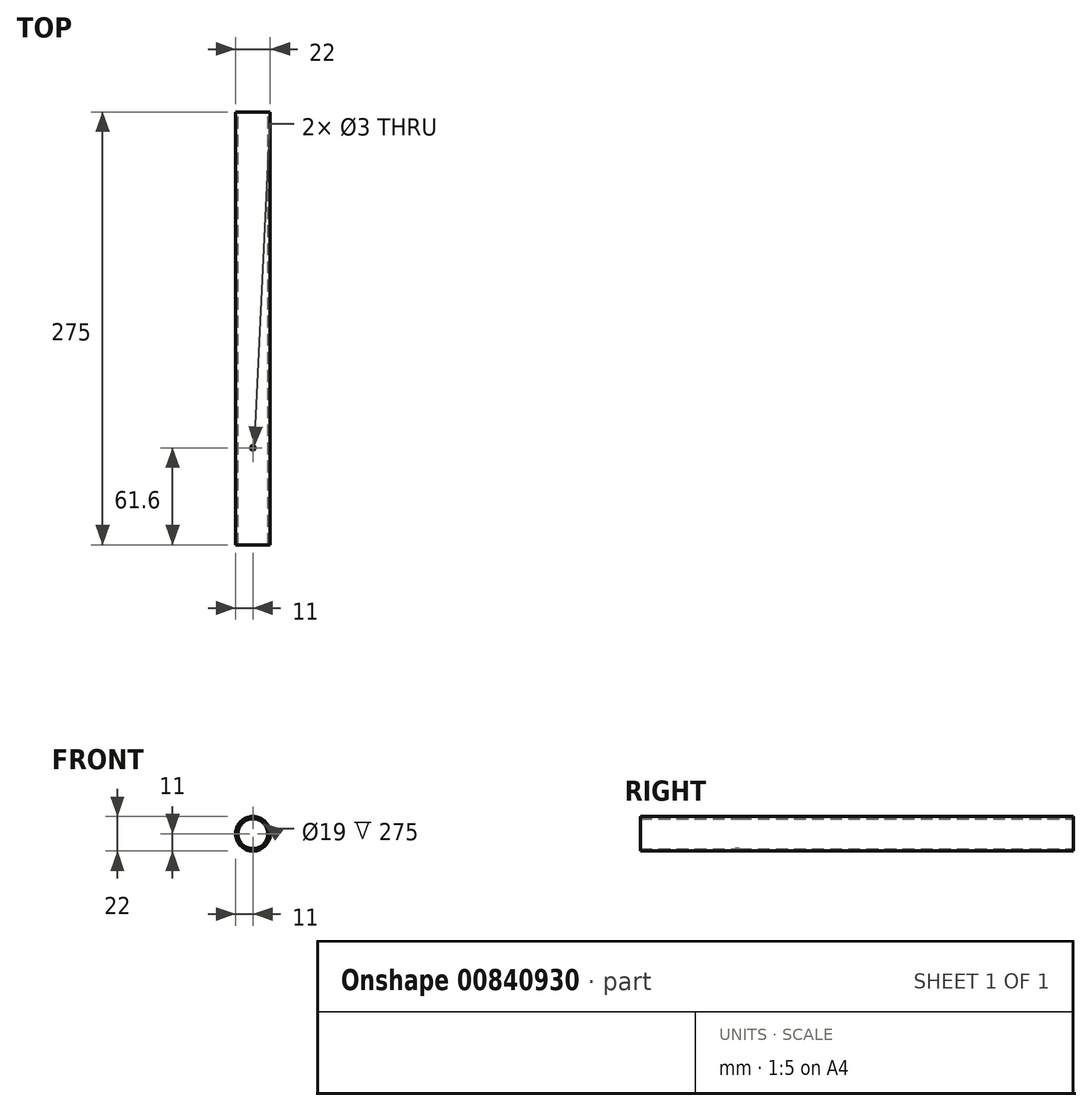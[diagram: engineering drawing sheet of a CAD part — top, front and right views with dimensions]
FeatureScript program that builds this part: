
annotation { "Feature Type Name" : "Feature", "Feature Type Description" : "" }
export const myFeature = defineFeature(function(context is Context, id is Id, definition is map)
    precondition{}
    {
        {
            var Q0;
            Q0=qCreatedBy(makeId("Front.planeOp"),FACE);
            var sketch = newSketch(context, id + "F0", { "sketchPlane" : qUnion([Q0])});
            skCircle(sketch, "E0", {"center": v(0, 0) * mm, "radius": 11 * mm});
            skCircle(sketch, "E1", {"center": v(0, 0) * mm, "radius": 9.5 * mm});
            skSolve(sketch);
        }
        {
            var Q0;
            Q0=qSketchRegion(id+"F0",true);
            extrude(context, id + "F1", {"entities" : qUnion([Q0]), "endBound" : BoundingType.SYMMETRIC, "depth" : 275 * mm, "offsetDistance" : 25 * mm});
        }
        {
            var Q0;
            Q0=qCreatedBy(makeId("Top.planeOp"),FACE);
            var sketch = newSketch(context, id + "F2", { "sketchPlane" : qUnion([Q0])});
            skCircle(sketch, "E2", {"center": v(0, -75.9) * mm, "radius": 1.5 * mm});
            skSolve(sketch);
        }
        {
            var Q0;
            Q0=qSketchRegion(id+"F2",true);
            extrude(context, id + "F3", {"entities" : qUnion([Q0]), "operationType" : NewBodyOperationType.REMOVE, "endBound" : BoundingType.SYMMETRIC, "oppositeDirection" : true, "depth" : 25 * mm, "offsetDistance" : 25 * mm});
        }
    });
